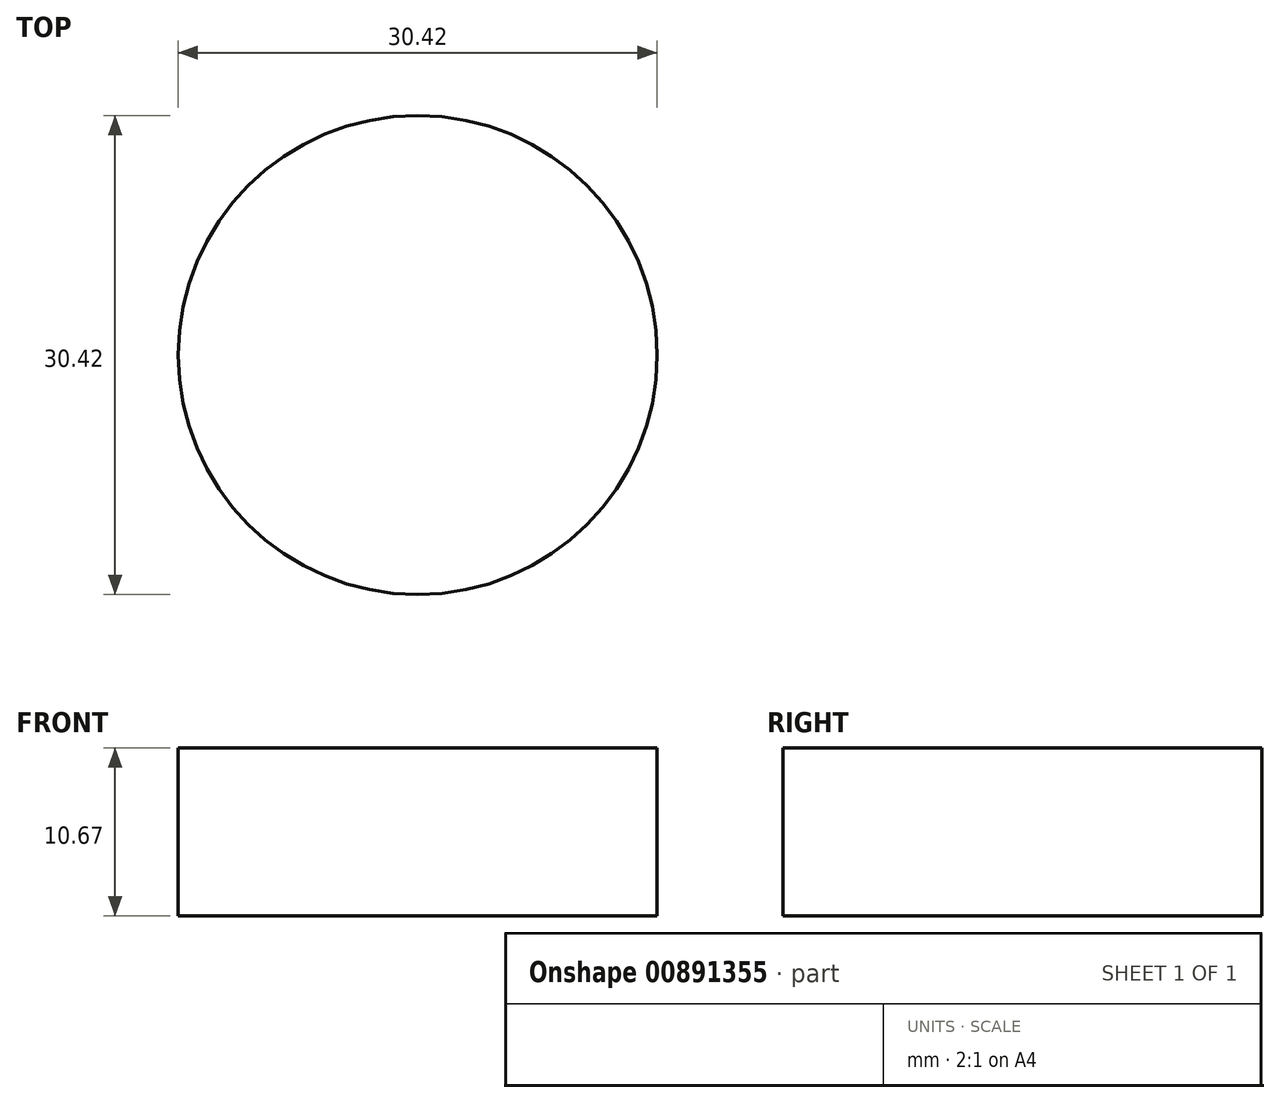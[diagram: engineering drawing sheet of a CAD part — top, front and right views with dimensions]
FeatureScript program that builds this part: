
annotation { "Feature Type Name" : "Feature", "Feature Type Description" : "" }
export const myFeature = defineFeature(function(context is Context, id is Id, definition is map)
    precondition{}
    {
        {
            var Q0;
            Q0=qCreatedBy(makeId("Top.planeOp"),FACE);
            var sketch = newSketch(context, id + "F0", { "sketchPlane" : qUnion([Q0])});
            skCircle(sketch, "E0", {"center": v(0, 0) * mm, "radius": 15.21 * mm});
            skSolve(sketch);
        }
        {
            var Q0;
            Q0 = qSketchRegion(id + "F0", true);
            extrude(context, id + "F1", {"entities" : qUnion([Q0]), "depth" : 10.67 * mm, "offsetDistance" : 25.4 * mm});
        }
    });
